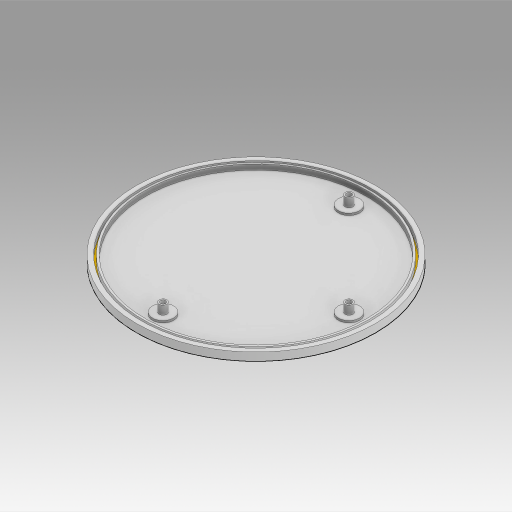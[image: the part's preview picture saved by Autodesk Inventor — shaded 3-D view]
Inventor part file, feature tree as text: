
AUTODESK INVENTOR PART (.ipt)
format: ipt  version: 2023 (Build 270158000, 158)  size: 232,448 bytes
history: native  units: mm
features: extrude x6, sketch x4, projected_geometry x1
ambient origin geometry x8: Origin, YZ Plane, XZ Plane, XY Plane, X Axis, Y Axis, Z Axis, Center Point
bodies: Solid1 (feature_tree)
feature tree (11):
  extrude  "Extrusion1"  Depth=3.0mm TaperAngle=0.0deg
  sketch  "Sketch2"  dims[d3=2.5mm d4=0.75mm]
  extrude  "Extrusion2"  Depth=0.75mm
  extrude  "Extrusion3"  Depth=2.0mm TaperAngle=0.0deg
  sketch  "Sketch3"  dims[d5=0.75mm d6=2.0mm d7=0.0mm]
  extrude  "Extrusion4"  Depth=4.0mm
  extrude  "Extrusion6"  Depth=3.0mm
  extrude  "Extrusion7"  Depth=3.0mm
  sketch  "Sketch1"  dims[d0=90.0mm d1=3.0mm d2=0.0mm]
  projected_geometry  "Projected Loop1"
  sketch  "Sketch5"  dims[d8=2.0mm d9=0.0mm d10=80.0mm d12=3.0mm d13=3.0mm d14=5.0mm d15=5.0mm d17=3.0mm d18=5.0mm d19=2.5mm d20=2.5mm d21=2.5mm d22=0.75mm d23=0.0mm d28=4.0mm d29=0.0mm d30=0.5mm d31=0.5mm d32=0.5mm d33=0.0mm d34=0.0mm d26=0.5mm d27=0.872665mm]
